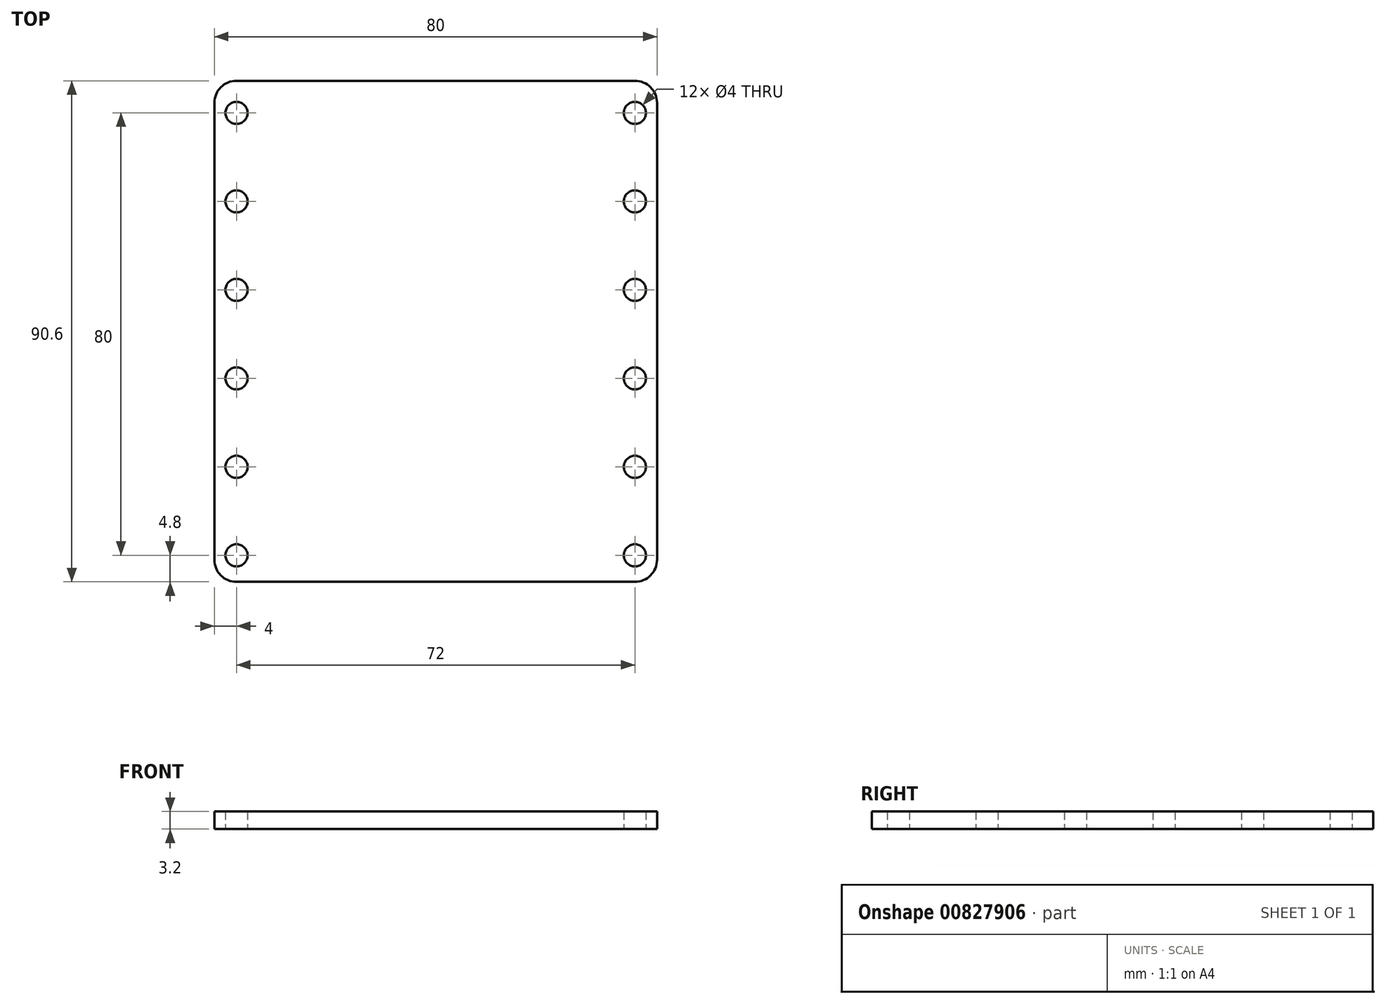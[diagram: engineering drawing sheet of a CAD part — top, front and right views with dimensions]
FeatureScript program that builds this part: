
annotation { "Feature Type Name" : "Feature", "Feature Type Description" : "" }
export const myFeature = defineFeature(function(context is Context, id is Id, definition is map)
    precondition{}
    {
        {
            var Q0;
            Q0=qCreatedBy(makeId("Top.planeOp"),FACE);
            var sketch = newSketch(context, id + "F0", { "sketchPlane" : qUnion([Q0])});
            skLineSegment(sketch, "E0.bottom", {"start": v(4, 0) * mm, "end": v(76, 0) * mm});
            skLineSegment(sketch, "E0.top", {"start": v(4, 90.6) * mm, "end": v(76, 90.6) * mm});
            skLineSegment(sketch, "E0.left", {"start": v(0, 4) * mm, "end": v(0, 86.6) * mm});
            skLineSegment(sketch, "E0.right", {"start": v(80, 4) * mm, "end": v(80, 86.6) * mm});
            skCircle(sketch, "E1", {"center": v(4, 4.8) * mm, "radius": 2 * mm});
            skCircle(sketch, "E2.0.1.0", {"center": v(4, 20.8) * mm, "radius": 2 * mm});
            skCircle(sketch, "E2.0.2.0", {"center": v(4, 36.8) * mm, "radius": 2 * mm});
            skCircle(sketch, "E2.0.3.0", {"center": v(4, 52.8) * mm, "radius": 2 * mm});
            skCircle(sketch, "E2.0.4.0", {"center": v(4, 68.8) * mm, "radius": 2 * mm});
            skCircle(sketch, "E2.0.5.0", {"center": v(4, 84.8) * mm, "radius": 2 * mm});
            skCircle(sketch, "E2.1.0.0", {"center": v(76, 4.8) * mm, "radius": 2 * mm});
            skCircle(sketch, "E2.1.1.0", {"center": v(76, 20.8) * mm, "radius": 2 * mm});
            skCircle(sketch, "E2.1.2.0", {"center": v(76, 36.8) * mm, "radius": 2 * mm});
            skCircle(sketch, "E2.1.3.0", {"center": v(76, 52.8) * mm, "radius": 2 * mm});
            skCircle(sketch, "E2.1.4.0", {"center": v(76, 68.8) * mm, "radius": 2 * mm});
            skCircle(sketch, "E2.1.5.0", {"center": v(76, 84.8) * mm, "radius": 2 * mm});
            skLineSegment(sketch, "E2.direction1", {"start": v(4, 4.8) * mm, "end": v(76, 4.8) * mm, "construction": true});
            skLineSegment(sketch, "E2.direction2", {"start": v(4, 4.8) * mm, "end": v(4, 20.8) * mm, "construction": true});
            skPoint(sketch, "E3.visualSharp", {"position": v(0, 90.6) * mm});
            skArc(sketch, "E3.filletArc", {"start": v(4, 90.6) * mm, "mid": v(1.17, 89.43) * mm, "end": v(0, 86.6) * mm});
            skPoint(sketch, "E4.visualSharp", {"position": v(80, 90.6) * mm});
            skArc(sketch, "E4.filletArc", {"start": v(80, 86.6) * mm, "mid": v(78.83, 89.43) * mm, "end": v(76, 90.6) * mm});
            skPoint(sketch, "E5.visualSharp", {"position": v(80, 0) * mm});
            skArc(sketch, "E5.filletArc", {"start": v(76, 0) * mm, "mid": v(78.83, 1.17) * mm, "end": v(80, 4) * mm});
            skPoint(sketch, "E6.visualSharp", {"position": v(0, 0) * mm});
            skArc(sketch, "E6.filletArc", {"start": v(0, 4) * mm, "mid": v(1.17, 1.17) * mm, "end": v(4, 0) * mm});
            skSolve(sketch);
        }
        {
            var Q0;
            Q0 = qSketchRegion(id + "F0", true);
            extrude(context, id + "F1", {"entities" : qUnion([Q0]), "depth" : 3.2 * mm, "offsetDistance" : 25 * mm});
        }
    });
